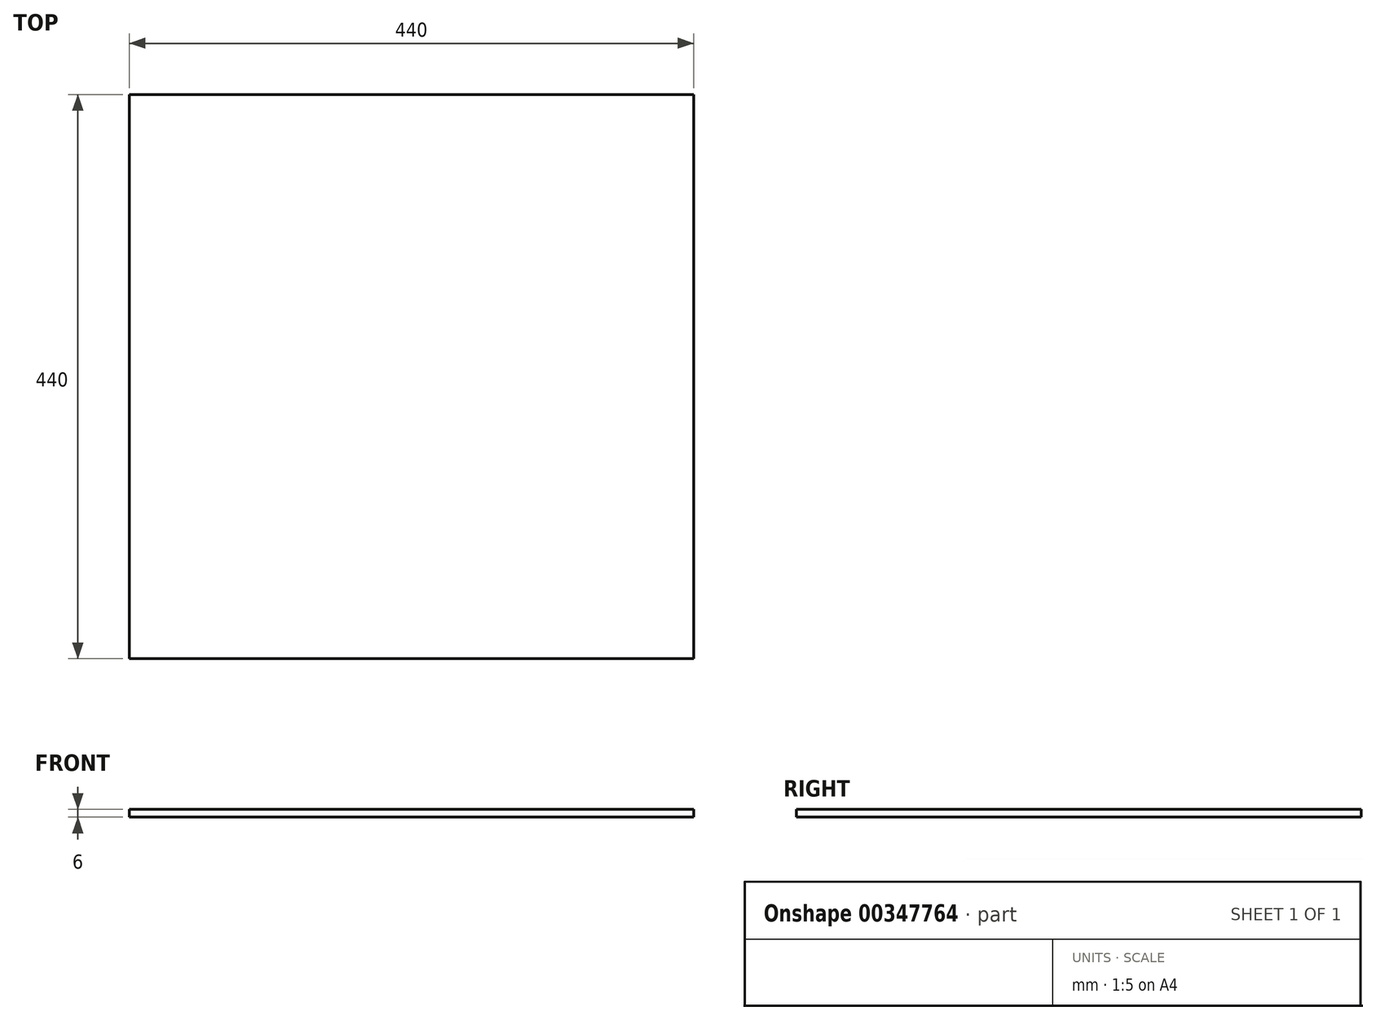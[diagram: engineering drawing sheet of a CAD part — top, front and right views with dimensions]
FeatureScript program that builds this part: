
annotation { "Feature Type Name" : "Feature", "Feature Type Description" : "" }
export const myFeature = defineFeature(function(context is Context, id is Id, definition is map)
    precondition{}
    {
        {
            var Q0;
            Q0=qCreatedBy(makeId("Top.planeOp"),FACE);
            var sketch = newSketch(context, id + "F0", { "sketchPlane" : qUnion([Q0])});
            skLineSegment(sketch, "E0.bottom", {"start": v(220, -220) * mm, "end": v(-220, -220) * mm});
            skLineSegment(sketch, "E0.top", {"start": v(220, 220) * mm, "end": v(-220, 220) * mm});
            skLineSegment(sketch, "E0.left", {"start": v(220, -220) * mm, "end": v(220, 220) * mm});
            skLineSegment(sketch, "E0.right", {"start": v(-220, -220) * mm, "end": v(-220, 220) * mm});
            skPoint(sketch, "E0.middle", {"position": v(0, 0) * mm});
            skSolve(sketch);
        }
        {
            var Q0;
            Q0=makeQuery(id+"F0.imprint","IMPRINT",FACE,{"disambiguationData":[TD([[makeQuery(id+"F0.imprint","IMPRINT",EDGE,{"derivedFrom":sQuery(id+"F0.wireOp",EDGE,"E0.bottom")}),-1.0]])]});
            extrude(context, id + "F1", {"entities" : qUnion([Q0]), "depth" : 6 * mm});
        }
    });
